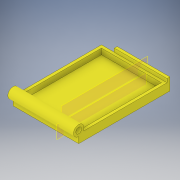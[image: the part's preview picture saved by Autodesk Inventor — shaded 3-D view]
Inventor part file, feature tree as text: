
AUTODESK INVENTOR PART (.ipt)
format: ipt  version: 2017 SP1 (Build 210196100, 196)  size: 179,712 bytes
history: native  units: in
note: dims shown in document units (in); Inventor stores cm internally (conversion verified against a paired STEP export)
features: extrude x7, sketch x7, plane x2, mirror x1
ambient origin geometry x8: Origin, YZ Plane, XZ Plane, XY Plane, X Axis, Y Axis, Z Axis, Center Point
bodies: Solid1 (feature_tree)
feature tree (17):
  extrude  "Extrusion1"  Depth=3.5in
  extrude  "Extrusion2"  TaperAngle=0.0deg  [1 undecoded]
  extrude  "Extrusion6"  Depth=3.875in
  extrude  "Extrusion7"  TaperAngle=0.0deg  [1 undecoded]
  extrude  "Extrusion8"  Depth=0.125in
  extrude  "Extrusion9"  TaperAngle=0.0deg  [1 undecoded]
  plane  "Work Plane1"
  extrude  "Extrusion10"  TaperAngle=0.0deg  [1 undecoded]
  plane  "Work Plane2"
  mirror  "Mirror1"
  sketch  "Sketch2"  dims[d0=2.5in d1=3.5in]
  sketch  "Sketch3"  dims[d2=0.75in d3=0.0in]
  sketch  "Sketch5"  dims[d4=2.875in d5=3.875in]
  sketch  "Sketch6"  dims[d6=0.125in d7=0.0in]
  sketch  "Sketch9"  dims[d8=0.125in d9=0.125in]
  sketch  "Sketch10"  dims[d10=0.375in d11=0.0in]
  sketch  "Sketch11"  dims[d15=0.0in d16=0.0in d17=0.0in d20=0.4531in d24=2.875in d25=0.0in d26=0.125in d27=2.875in d28=0.0in d29=0.125in d30=0.0in d31=0.531in d32=0.125in d33=0.0in d34=-0.6565in d35=0.25in d36=1.0in d37=0.0in d38=-1.1565in]
note: 4 required parameter values undecoded (feature->parameter linkage not recoverable at this tier; creation-order binding heuristic only, values carry confidence <= 0.55)
